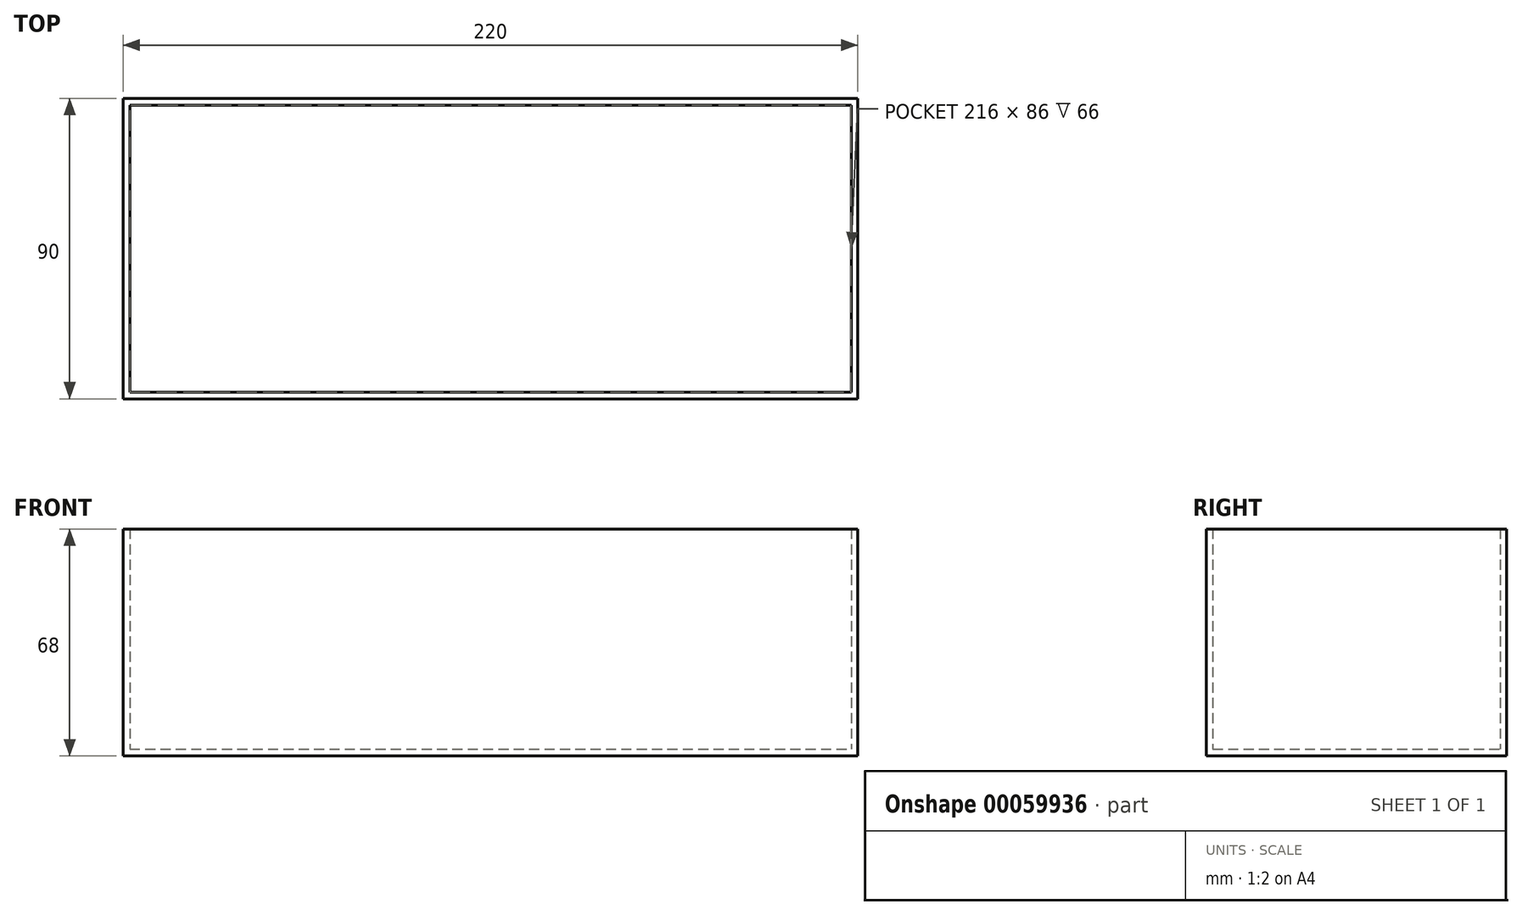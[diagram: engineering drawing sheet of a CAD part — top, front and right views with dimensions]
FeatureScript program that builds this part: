
annotation { "Feature Type Name" : "Feature", "Feature Type Description" : "" }
export const myFeature = defineFeature(function(context is Context, id is Id, definition is map)
    precondition{}
    {
        {
            var Q0;
            Q0=qCreatedBy(makeId("Top.planeOp"),FACE);
            var sketch = newSketch(context, id + "F0", { "sketchPlane" : qUnion([Q0])});
            skLineSegment(sketch, "E0.bottom", {"start": v(0, 0) * mm, "end": v(220, 0) * mm});
            skLineSegment(sketch, "E0.top", {"start": v(0, 90) * mm, "end": v(220, 90) * mm});
            skLineSegment(sketch, "E0.left", {"start": v(0, 0) * mm, "end": v(0, 90) * mm});
            skLineSegment(sketch, "E0.right", {"start": v(220, 0) * mm, "end": v(220, 90) * mm});
            skLineSegment(sketch, "E1.bottom", {"start": v(2, 2) * mm, "end": v(218, 2) * mm});
            skLineSegment(sketch, "E1.top", {"start": v(2, 88) * mm, "end": v(218, 88) * mm});
            skLineSegment(sketch, "E1.left", {"start": v(2, 2) * mm, "end": v(2, 88) * mm});
            skLineSegment(sketch, "E1.right", {"start": v(218, 2) * mm, "end": v(218, 88) * mm});
            skLineSegment(sketch, "E2", {"start": v(2, 2) * mm, "end": v(0, 2) * mm, "construction": true});
            skLineSegment(sketch, "E3", {"start": v(2, 2) * mm, "end": v(2, 0) * mm, "construction": true});
            skLineSegment(sketch, "E4", {"start": v(218, 88) * mm, "end": v(218, 90) * mm, "construction": true});
            skLineSegment(sketch, "E5", {"start": v(218, 88) * mm, "end": v(220, 88) * mm, "construction": true});
            skSolve(sketch);
        }
        {
            var Q0;
            {var subQ1=sQuery(id+"F0.wireOp",EDGE,"E0.bottom");Q0=makeQuery(id+"F0.imprint","IMPRINT",FACE,{"disambiguationData":[TD([[makeQuery(id+"F0.imprint","IMPRINT",EDGE,{"derivedFrom":subQ1}),1.0]])]});}
            extrude(context, id + "F1", {"entities" : qUnion([Q0]), "depth" : 68 * mm});
        }
        {
            var Q0;
            Q0=qCreatedBy(makeId("Top.planeOp"),FACE);
            var sketch = newSketch(context, id + "F2", { "sketchPlane" : qUnion([Q0])});
            skLineSegment(sketch, "E6.bottom", {"start": v(0, 0) * mm, "end": v(220, 0) * mm});
            skLineSegment(sketch, "E6.top", {"start": v(0, 90) * mm, "end": v(220, 90) * mm});
            skLineSegment(sketch, "E6.left", {"start": v(0, 0) * mm, "end": v(0, 90) * mm});
            skLineSegment(sketch, "E6.right", {"start": v(220, 0) * mm, "end": v(220, 90) * mm});
            skSolve(sketch);
        }
        {
            var Q0;
            Q0 = qSketchRegion(id + "F2", true);
            extrude(context, id + "F3", {"entities" : qUnion([Q0]), "operationType" : NewBodyOperationType.ADD, "depth" : 2 * mm});
        }
    });
